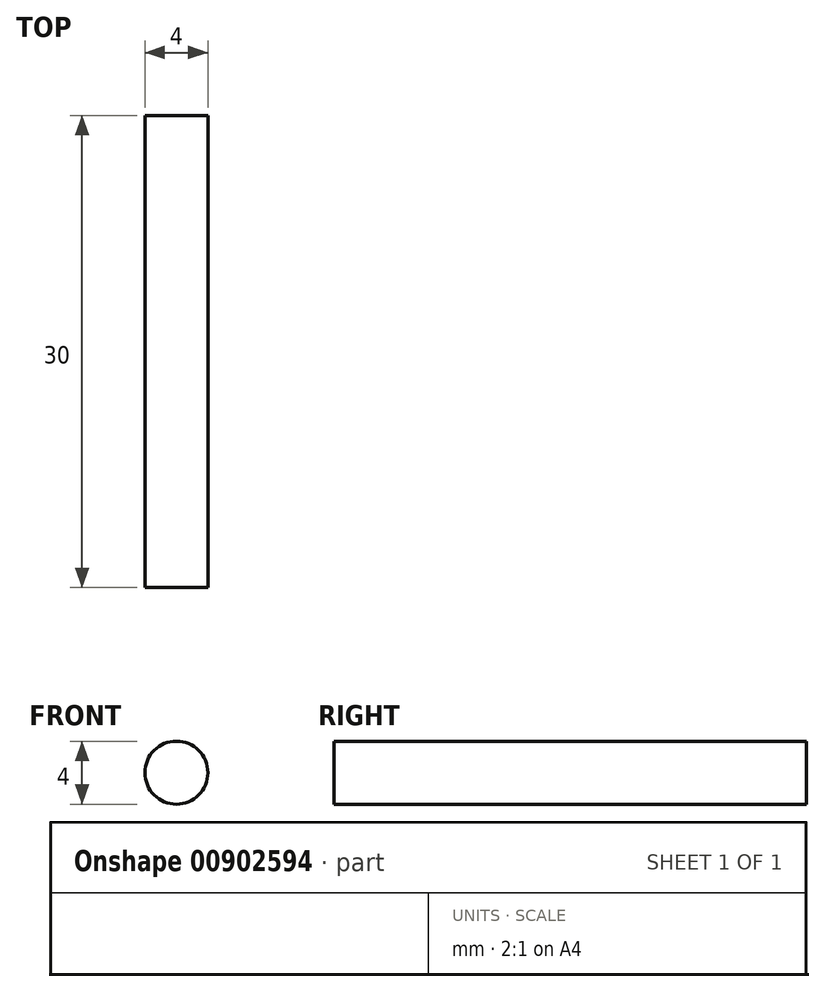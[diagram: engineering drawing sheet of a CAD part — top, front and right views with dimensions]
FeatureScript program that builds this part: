
annotation { "Feature Type Name" : "Feature", "Feature Type Description" : "" }
export const myFeature = defineFeature(function(context is Context, id is Id, definition is map)
    precondition{}
    {
        {
            var Q0;
            Q0=qCreatedBy(makeId("Front.planeOp"),FACE);
            var sketch = newSketch(context, id + "F0", { "sketchPlane" : qUnion([Q0])});
            skCircle(sketch, "E0", {"center": v(0, 0) * mm, "radius": 2 * mm});
            skSolve(sketch);
        }
        {
            var Q0;
            Q0 = qSketchRegion(id + "F0", true);
            extrude(context, id + "F1", {"entities" : qUnion([Q0]), "endBound" : BoundingType.SYMMETRIC, "depth" : 30 * mm, "offsetDistance" : 25 * mm});
        }
    });
